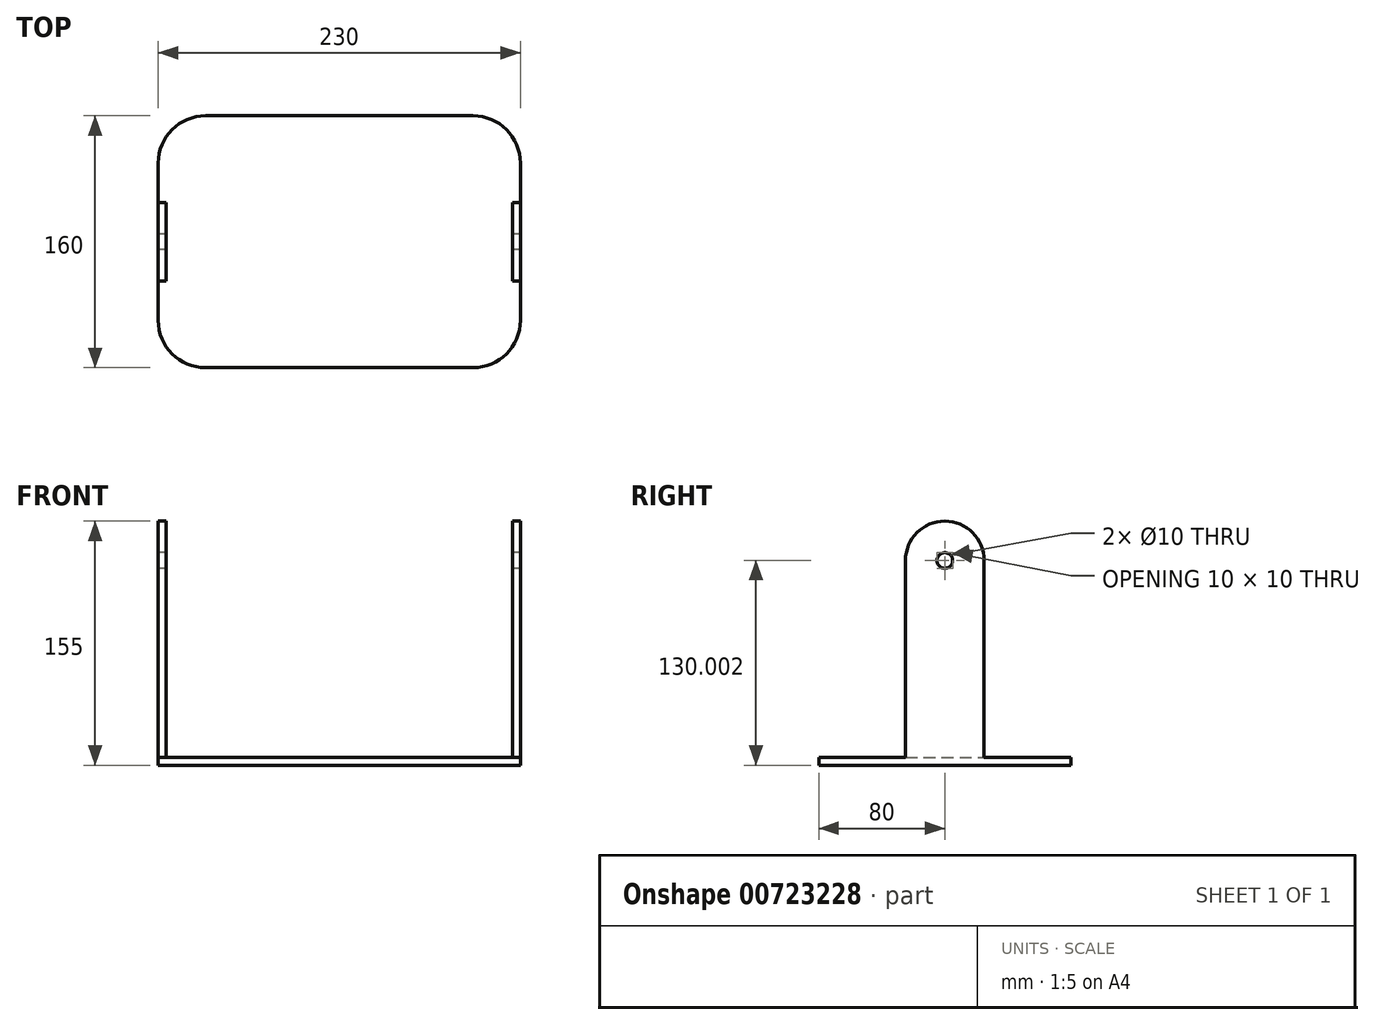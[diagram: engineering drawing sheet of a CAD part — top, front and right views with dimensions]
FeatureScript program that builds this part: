
annotation { "Feature Type Name" : "Feature", "Feature Type Description" : "" }
export const myFeature = defineFeature(function(context is Context, id is Id, definition is map)
    precondition{}
    {
        {
            var Q0;
            Q0=qCreatedBy(makeId("Front.planeOp"),FACE);
            var sketch = newSketch(context, id + "F0", { "sketchPlane" : qUnion([Q0])});
            skLineSegment(sketch, "E0.bottom", {"start": v(-119.92, -82.57) * mm, "end": v(110.08, -82.57) * mm});
            skLineSegment(sketch, "E0.top", {"start": v(-119.92, 72.43) * mm, "end": v(-114.92, 72.43) * mm});
            skLineSegment(sketch, "E0.left", {"start": v(-119.92, -82.57) * mm, "end": v(-119.92, 72.43) * mm});
            skLineSegment(sketch, "E0.right", {"start": v(110.08, -82.57) * mm, "end": v(110.08, 72.43) * mm});
            skLineSegment(sketch, "E1.top", {"start": v(-114.92, -77.57) * mm, "end": v(105.08, -77.57) * mm});
            skLineSegment(sketch, "E1.left", {"start": v(-114.92, 72.43) * mm, "end": v(-114.92, -77.57) * mm});
            skLineSegment(sketch, "E1.right", {"start": v(105.08, 72.43) * mm, "end": v(105.08, -77.57) * mm});
            skLineSegment(sketch, "E2.trimOffspring", {"start": v(105.08, 72.43) * mm, "end": v(110.08, 72.43) * mm});
            skSolve(sketch);
        }
        {
            var Q0;
            Q0 = qSketchRegion(id + "F0", true);
            extrude(context, id + "F1", {"entities" : qUnion([Q0]), "depth" : 50 * mm, "offsetDistance" : 25 * mm});
        }
        {
            var Q0;
            Q0=makeQuery(id+"F1.opExtrude","CAP_EDGE",EDGE,{"disambiguationData":[OSD([sQuery(id+"F0.wireOp",EDGE,"E0.top")])],"isStart":false});
            var Q1;
            Q1=makeQuery(id+"F1.opExtrude","CAP_EDGE",EDGE,{"disambiguationData":[OSD([sQuery(id+"F0.wireOp",EDGE,"E0.top")])],"isStart":true});
            var Q2;
            Q2=makeQuery(id+"F1.opExtrude","CAP_EDGE",EDGE,{"disambiguationData":[OSD([sQuery(id+"F0.wireOp",EDGE,"E2.trimOffspring")])],"isStart":false});
            var Q3;
            Q3=makeQuery(id+"F1.opExtrude","CAP_EDGE",EDGE,{"disambiguationData":[OSD([sQuery(id+"F0.wireOp",EDGE,"E2.trimOffspring")])],"isStart":true});
            fillet(context, id + "F2", {"entities" : qUnion([Q0, Q1, Q2, Q3]), "radius" : 25 * mm, "tangentPropagation" : true, "allowEdgeOverflow" : false});
        }
        {
            var Q0;
            Q0=makeQuery(id+"F1.opExtrude","SWEPT_FACE",FACE,{"disambiguationData":[OSD([sQuery(id+"F0.wireOp",EDGE,"E0.left")])]});
            var sketch = newSketch(context, id + "F3", { "sketchPlane" : qUnion([Q0])});
            skCircle(sketch, "E3", {"center": v(25, 47.43) * mm, "radius": 5 * mm});
            skSolve(sketch);
        }
        {
            var Q0;
            Q0 = qSketchRegion(id + "F3", true);
            extrude(context, id + "F4", {"entities" : qUnion([Q0]), "operationType" : NewBodyOperationType.REMOVE, "endBound" : BoundingType.THROUGH_ALL, "oppositeDirection" : true, "depth" : 25 * mm, "offsetDistance" : 25 * mm});
        }
        {
            var Q0;
            Q0=makeQuery(id+"F1.opExtrude","SWEPT_FACE",FACE,{"disambiguationData":[OSD([sQuery(id+"F0.wireOp",EDGE,"E0.bottom")])]});
            var sketch = newSketch(context, id + "F5", { "sketchPlane" : qUnion([Q0])});
            skLineSegment(sketch, "E4.bottom", {"start": v(-89.92, 105) * mm, "end": v(80.08, 105) * mm});
            skLineSegment(sketch, "E4.top", {"start": v(-89.92, -55) * mm, "end": v(80.08, -55) * mm});
            skLineSegment(sketch, "E4.left", {"start": v(-119.92, 75) * mm, "end": v(-119.92, -25) * mm});
            skLineSegment(sketch, "E4.right", {"start": v(110.08, 75) * mm, "end": v(110.08, -25) * mm});
            skPoint(sketch, "E5.visualSharp", {"position": v(-119.92, -55) * mm});
            skArc(sketch, "E5.filletArc", {"start": v(-119.92, -25) * mm, "mid": v(-111.13, -46.21) * mm, "end": v(-89.92, -55) * mm});
            skPoint(sketch, "E6.visualSharp", {"position": v(110.08, -55) * mm});
            skArc(sketch, "E6.filletArc", {"start": v(80.08, -55) * mm, "mid": v(101.3, -46.21) * mm, "end": v(110.08, -25) * mm});
            skPoint(sketch, "E7.visualSharp", {"position": v(110.08, 105) * mm});
            skArc(sketch, "E7.filletArc", {"start": v(110.08, 75) * mm, "mid": v(101.3, 96.21) * mm, "end": v(80.08, 105) * mm});
            skPoint(sketch, "E8.visualSharp", {"position": v(-119.92, 105) * mm});
            skArc(sketch, "E8.filletArc", {"start": v(-89.92, 105) * mm, "mid": v(-111.13, 96.21) * mm, "end": v(-119.92, 75) * mm});
            skSolve(sketch);
        }
        {
            var Q0;
            Q0 = qSketchRegion(id + "F5", true);
            extrude(context, id + "F6", {"entities" : qUnion([Q0]), "operationType" : NewBodyOperationType.ADD, "oppositeDirection" : true, "depth" : 5 * mm, "offsetDistance" : 25 * mm});
        }
    });
